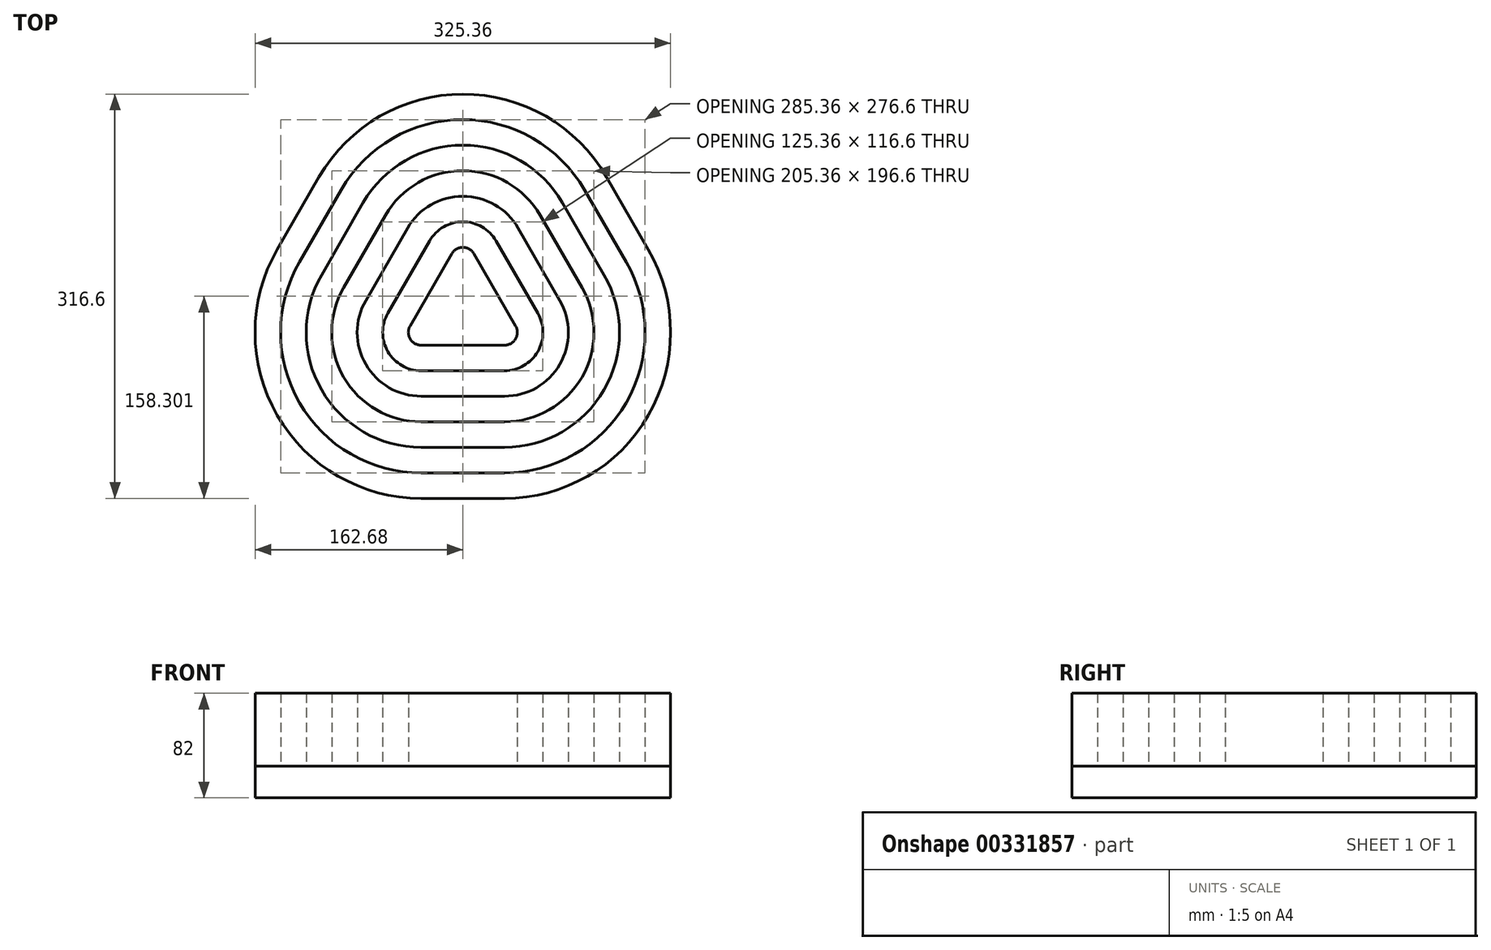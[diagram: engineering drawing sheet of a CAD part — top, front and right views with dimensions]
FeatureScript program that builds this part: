
annotation { "Feature Type Name" : "Feature", "Feature Type Description" : "" }
export const myFeature = defineFeature(function(context is Context, id is Id, definition is map)
    precondition{}
    {
        {
            var Q0;
            Q0=qCreatedBy(makeId("Top.planeOp"),FACE);
            var sketch = newSketch(context, id + "F0", { "sketchPlane" : qUnion([Q0])});
            skLineSegment(sketch, "E0", {"start": v(-8.66, 32.4) * mm, "end": v(-41.34, -24.2) * mm});
            skLineSegment(sketch, "E1", {"start": v(-32.68, -39.2) * mm, "end": v(32.68, -39.2) * mm});
            skLineSegment(sketch, "E2", {"start": v(41.34, -24.2) * mm, "end": v(8.66, 32.4) * mm});
            skPoint(sketch, "E3.visualSharp", {"position": v(0, 47.4) * mm});
            skArc(sketch, "E3.filletArc", {"start": v(8.66, 32.4) * mm, "mid": v(0, 37.4) * mm, "end": v(-8.66, 32.4) * mm});
            skPoint(sketch, "E4.visualSharp", {"position": v(-50, -39.2) * mm});
            skArc(sketch, "E4.filletArc", {"start": v(-41.34, -24.2) * mm, "mid": v(-41.34, -34.2) * mm, "end": v(-32.68, -39.2) * mm});
            skPoint(sketch, "E5.visualSharp", {"position": v(50, -39.2) * mm});
            skArc(sketch, "E5.filletArc", {"start": v(32.68, -39.2) * mm, "mid": v(41.34, -34.2) * mm, "end": v(41.34, -24.2) * mm});
            skArc(sketch, "E6.0", {"start": v(25.98, 42.4) * mm, "mid": v(0, 57.4) * mm, "end": v(-25.98, 42.4) * mm});
            skArc(sketch, "E6.1", {"start": v(-58.66, -14.2) * mm, "mid": v(-58.66, -44.2) * mm, "end": v(-32.68, -59.2) * mm});
            skLineSegment(sketch, "E6.2", {"start": v(-32.68, -59.2) * mm, "end": v(32.68, -59.2) * mm});
            skLineSegment(sketch, "E6.3", {"start": v(-25.98, 42.4) * mm, "end": v(-58.66, -14.2) * mm});
            skArc(sketch, "E6.4", {"start": v(32.68, -59.2) * mm, "mid": v(58.66, -44.2) * mm, "end": v(58.66, -14.2) * mm});
            skLineSegment(sketch, "E6.5", {"start": v(58.66, -14.2) * mm, "end": v(25.98, 42.4) * mm});
            skArc(sketch, "E7.0", {"start": v(43.3, 52.4) * mm, "mid": v(0, 77.4) * mm, "end": v(-43.3, 52.4) * mm});
            skArc(sketch, "E7.1", {"start": v(-75.98, -4.2) * mm, "mid": v(-75.98, -54.2) * mm, "end": v(-32.68, -79.2) * mm});
            skLineSegment(sketch, "E7.2", {"start": v(-32.68, -79.2) * mm, "end": v(32.68, -79.2) * mm});
            skLineSegment(sketch, "E7.3", {"start": v(-43.3, 52.4) * mm, "end": v(-75.98, -4.2) * mm});
            skArc(sketch, "E7.4", {"start": v(32.68, -79.2) * mm, "mid": v(75.98, -54.2) * mm, "end": v(75.98, -4.2) * mm});
            skLineSegment(sketch, "E7.5", {"start": v(75.98, -4.2) * mm, "end": v(43.3, 52.4) * mm});
            skArc(sketch, "E8.0", {"start": v(60.62, 62.4) * mm, "mid": v(0, 97.4) * mm, "end": v(-60.62, 62.4) * mm});
            skArc(sketch, "E8.1", {"start": v(-93.3, 5.8) * mm, "mid": v(-93.3, -64.2) * mm, "end": v(-32.68, -99.2) * mm});
            skLineSegment(sketch, "E8.2", {"start": v(-32.68, -99.2) * mm, "end": v(32.68, -99.2) * mm});
            skLineSegment(sketch, "E8.3", {"start": v(-60.62, 62.4) * mm, "end": v(-93.3, 5.8) * mm});
            skArc(sketch, "E8.4", {"start": v(32.68, -99.2) * mm, "mid": v(93.3, -64.2) * mm, "end": v(93.3, 5.8) * mm});
            skLineSegment(sketch, "E8.5", {"start": v(93.3, 5.8) * mm, "end": v(60.62, 62.4) * mm});
            skArc(sketch, "E9.0", {"start": v(77.94, 72.4) * mm, "mid": v(0, 117.4) * mm, "end": v(-77.94, 72.4) * mm});
            skArc(sketch, "E9.1", {"start": v(-110.62, 15.8) * mm, "mid": v(-110.62, -74.2) * mm, "end": v(-32.68, -119.2) * mm});
            skLineSegment(sketch, "E9.2", {"start": v(-32.68, -119.2) * mm, "end": v(32.68, -119.2) * mm});
            skLineSegment(sketch, "E9.3", {"start": v(-77.94, 72.4) * mm, "end": v(-110.62, 15.8) * mm});
            skArc(sketch, "E9.4", {"start": v(32.68, -119.2) * mm, "mid": v(110.62, -74.2) * mm, "end": v(110.62, 15.8) * mm});
            skLineSegment(sketch, "E9.5", {"start": v(110.62, 15.8) * mm, "end": v(77.94, 72.4) * mm});
            skArc(sketch, "E10.0", {"start": v(95.26, 82.4) * mm, "mid": v(0, 137.4) * mm, "end": v(-95.26, 82.4) * mm});
            skArc(sketch, "E10.1", {"start": v(-127.94, 25.8) * mm, "mid": v(-127.94, -84.2) * mm, "end": v(-32.68, -139.2) * mm});
            skLineSegment(sketch, "E10.2", {"start": v(-32.68, -139.2) * mm, "end": v(32.68, -139.2) * mm});
            skLineSegment(sketch, "E10.3", {"start": v(-95.26, 82.4) * mm, "end": v(-127.94, 25.8) * mm});
            skArc(sketch, "E10.4", {"start": v(32.68, -139.2) * mm, "mid": v(127.94, -84.2) * mm, "end": v(127.94, 25.8) * mm});
            skLineSegment(sketch, "E10.5", {"start": v(127.94, 25.8) * mm, "end": v(95.26, 82.4) * mm});
            skArc(sketch, "E11.0", {"start": v(112.58, 92.4) * mm, "mid": v(0, 157.4) * mm, "end": v(-112.58, 92.4) * mm});
            skArc(sketch, "E11.1", {"start": v(-145.26, 35.8) * mm, "mid": v(-145.26, -94.2) * mm, "end": v(-32.68, -159.2) * mm});
            skLineSegment(sketch, "E11.2", {"start": v(-32.68, -159.2) * mm, "end": v(32.68, -159.2) * mm});
            skLineSegment(sketch, "E11.3", {"start": v(-112.58, 92.4) * mm, "end": v(-145.26, 35.8) * mm});
            skArc(sketch, "E11.4", {"start": v(32.68, -159.2) * mm, "mid": v(145.26, -94.2) * mm, "end": v(145.26, 35.8) * mm});
            skLineSegment(sketch, "E11.5", {"start": v(145.26, 35.8) * mm, "end": v(112.58, 92.4) * mm});
            skSolve(sketch);
        }
        {
            var Q0;
            Q0=makeQuery(id+"F0.imprint","IMPRINT",FACE,{"disambiguationData":[TD([[makeQuery(id+"F0.imprint","IMPRINT",EDGE,{"derivedFrom":sQuery(id+"F0.wireOp",EDGE,"E0")}),1.0]])]});
            var Q1;
            Q1=makeQuery(id+"F0.imprint","IMPRINT",FACE,{"disambiguationData":[TD([[makeQuery(id+"F0.imprint","IMPRINT",EDGE,{"derivedFrom":sQuery(id+"F0.wireOp",EDGE,"E6.0")}),-1.0]])]});
            var Q2;
            Q2=makeQuery(id+"F0.imprint","IMPRINT",FACE,{"disambiguationData":[TD([[makeQuery(id+"F0.imprint","IMPRINT",EDGE,{"derivedFrom":sQuery(id+"F0.wireOp",EDGE,"E8.0")}),-1.0]])]});
            var Q3;
            Q3=makeQuery(id+"F0.imprint","IMPRINT",FACE,{"disambiguationData":[TD([[makeQuery(id+"F0.imprint","IMPRINT",EDGE,{"derivedFrom":sQuery(id+"F0.wireOp",EDGE,"E10.0")}),-1.0]])]});
            extrude(context, id + "F1", {"entities" : qUnion([Q0, Q1, Q2, Q3]), "depth" : 57 * mm});
        }
        {
            var Q0;
            Q0=makeQuery(id+"F1.opExtrude","CAP_FACE",FACE,{"disambiguationData":[OSD([sQuery(id+"F0.wireOp",EDGE,"E10.0"),sQuery(id+"F0.wireOp",EDGE,"E10.1"),sQuery(id+"F0.wireOp",EDGE,"E10.2"),sQuery(id+"F0.wireOp",EDGE,"E10.3"),sQuery(id+"F0.wireOp",EDGE,"E10.4"),sQuery(id+"F0.wireOp",EDGE,"E10.5"),sQuery(id+"F0.wireOp",EDGE,"E11.0"),sQuery(id+"F0.wireOp",EDGE,"E11.1"),sQuery(id+"F0.wireOp",EDGE,"E11.2"),sQuery(id+"F0.wireOp",EDGE,"E11.3"),sQuery(id+"F0.wireOp",EDGE,"E11.4"),sQuery(id+"F0.wireOp",EDGE,"E11.5")])],"isStart":true});
            var sketch = newSketch(context, id + "F2", { "sketchPlane" : qUnion([Q0])});
            skArc(sketch, "E12.0", {"start": v(-145.26, -35.8) * mm, "mid": v(-145.26, 94.2) * mm, "end": v(-32.68, 159.2) * mm});
            skLineSegment(sketch, "E13.0", {"start": v(-32.68, 159.2) * mm, "end": v(32.68, 159.2) * mm});
            skArc(sketch, "E14.0", {"start": v(32.68, 159.2) * mm, "mid": v(145.26, 94.2) * mm, "end": v(145.26, -35.8) * mm});
            skLineSegment(sketch, "E15.0", {"start": v(145.26, -35.8) * mm, "end": v(112.58, -92.4) * mm});
            skArc(sketch, "E16.0", {"start": v(112.58, -92.4) * mm, "mid": v(0, -157.4) * mm, "end": v(-112.58, -92.4) * mm});
            skLineSegment(sketch, "E17.0", {"start": v(-112.58, -92.4) * mm, "end": v(-145.26, -35.8) * mm});
            skSolve(sketch);
        }
        {
            var Q0;
            Q0 = qSketchRegion(id + "F2", true);
            extrude(context, id + "F3", {"entities" : qUnion([Q0]), "depth" : 25 * mm});
        }
    });
